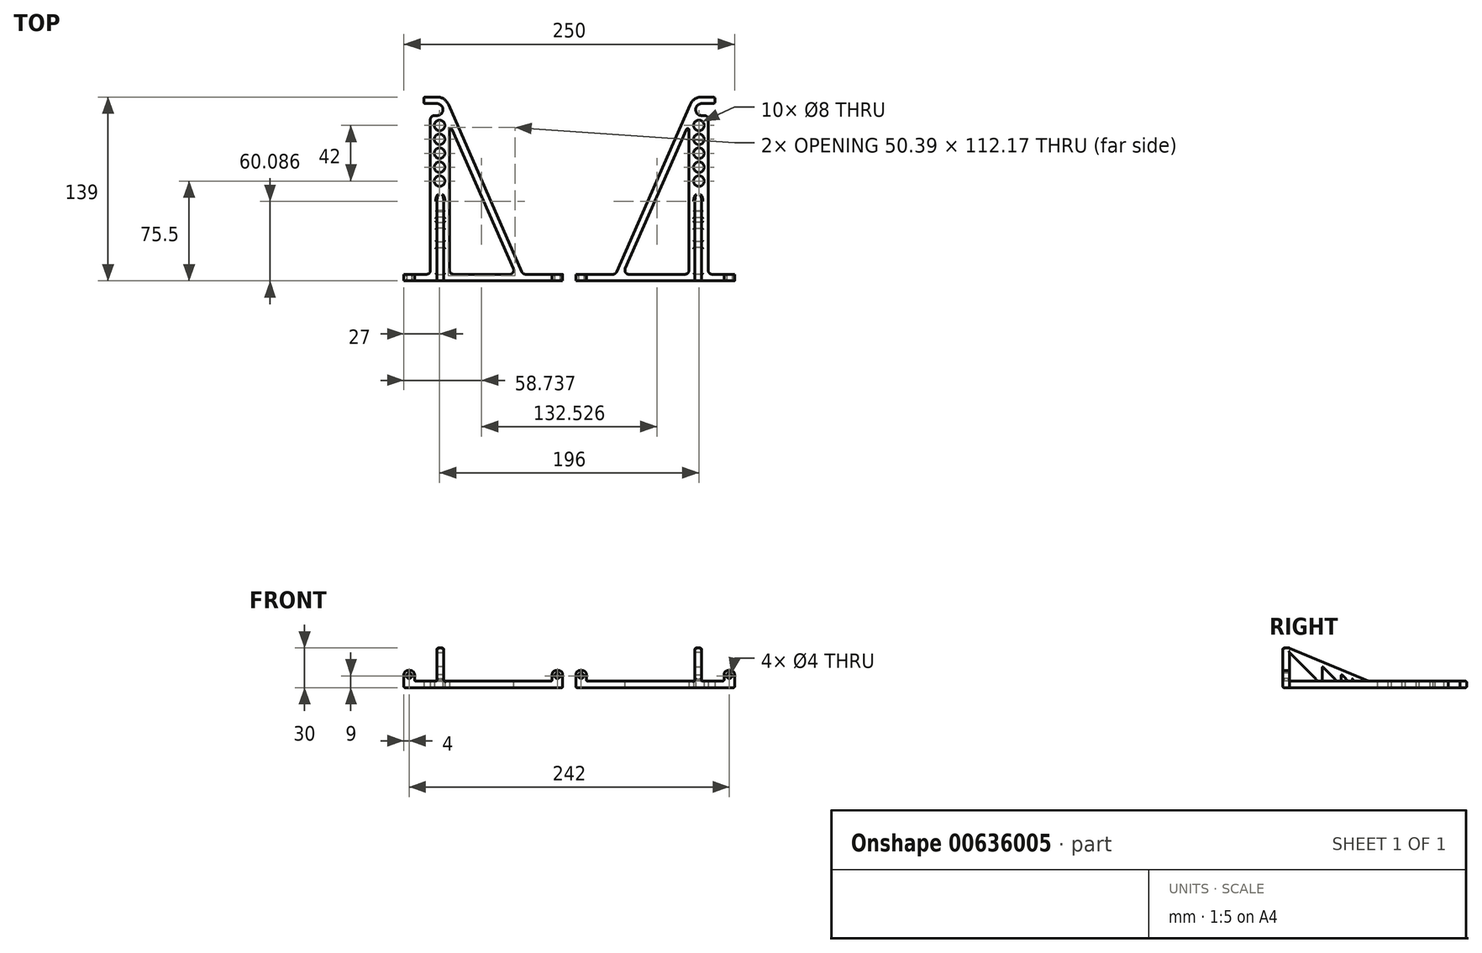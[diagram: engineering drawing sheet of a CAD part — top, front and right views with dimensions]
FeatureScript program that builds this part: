
annotation { "Feature Type Name" : "Feature", "Feature Type Description" : "" }
export const myFeature = defineFeature(function(context is Context, id is Id, definition is map)
    precondition{}
    {
        {
            var Q0;
            Q0=qCreatedBy(makeId("Top.planeOp"),FACE);
            var sketch = newSketch(context, id + "F0", { "sketchPlane" : qUnion([Q0])});
            skLineSegment(sketch, "E0", {"start": v(5, 0) * mm, "end": v(125, 0) * mm});
            skLineSegment(sketch, "E1", {"start": v(5, 0) * mm, "end": v(5, 5) * mm});
            skLineSegment(sketch, "E2", {"start": v(5, 5) * mm, "end": v(35, 5) * mm});
            skLineSegment(sketch, "E3", {"start": v(125, 5) * mm, "end": v(125, 0) * mm});
            skPoint(sketch, "E4", {"position": v(35, 5) * mm});
            skPoint(sketch, "E5", {"position": v(105, 5) * mm});
            skLineSegment(sketch, "E6", {"start": v(105, 5) * mm, "end": v(105, 125) * mm});
            skLineSegment(sketch, "E7", {"start": v(105, 125) * mm, "end": v(100, 125) * mm});
            skPoint(sketch, "E8", {"position": v(100, 134) * mm});
            skArc(sketch, "E9", {"start": v(100, 134) * mm, "mid": v(95.5, 129.5) * mm, "end": v(100, 125) * mm});
            skLineSegment(sketch, "E10", {"start": v(100, 134) * mm, "end": v(110, 134) * mm});
            skLineSegment(sketch, "E11", {"start": v(110, 134) * mm, "end": v(110, 139) * mm});
            skLineSegment(sketch, "E12", {"start": v(110, 139) * mm, "end": v(100, 139) * mm});
            skLineSegment(sketch, "E13", {"start": v(35, 5) * mm, "end": v(91.3, 133.32) * mm});
            skLineSegment(sketch, "E14.trimOffspring", {"start": v(105, 5) * mm, "end": v(125, 5) * mm});
            skArc(sketch, "E15", {"start": v(100, 139) * mm, "mid": v(94.8, 137.45) * mm, "end": v(91.3, 133.32) * mm});
            skLineSegment(sketch, "E16", {"start": v(40.46, 5) * mm, "end": v(90.46, 5) * mm});
            skLineSegment(sketch, "E17", {"start": v(90.46, 5) * mm, "end": v(90.46, 118.96) * mm});
            skLineSegment(sketch, "E18", {"start": v(90.46, 118.96) * mm, "end": v(40.46, 5) * mm});
            skPoint(sketch, "E19", {"position": v(98, 75.5) * mm});
            skCircle(sketch, "E20", {"center": v(98, 75.5) * mm, "radius": 4 * mm});
            skPoint(sketch, "E21", {"position": v(98, 86) * mm});
            skCircle(sketch, "E22", {"center": v(98, 86) * mm, "radius": 4 * mm});
            skPoint(sketch, "E23", {"position": v(98, 96.5) * mm});
            skPoint(sketch, "E24", {"position": v(98, 107) * mm});
            skCircle(sketch, "E25", {"center": v(98, 96.5) * mm, "radius": 4 * mm});
            skCircle(sketch, "E26", {"center": v(98, 107) * mm, "radius": 4 * mm});
            skPoint(sketch, "E27", {"position": v(98, 117.5) * mm});
            skCircle(sketch, "E28", {"center": v(98, 117.5) * mm, "radius": 4 * mm});
            skSolve(sketch);
        }
        {
            var Q0;
            Q0=makeQuery(id+"F0.imprint","IMPRINT",FACE,{"disambiguationData":[TD([[makeQuery(id+"F0.imprint","IMPRINT",EDGE,{"derivedFrom":sQuery(id+"F0.wireOp",EDGE,"E0")}),1.0]])]});
            extrude(context, id + "F1", {"entities" : qUnion([Q0]), "depth" : 5 * mm, "offsetDistance" : 25 * mm});
        }
        {
            var Q0;
            Q0=qCreatedBy(makeId("Front.planeOp"),FACE);
            var sketch = newSketch(context, id + "F2", { "sketchPlane" : qUnion([Q0])});
            skPoint(sketch, "E29", {"position": v(5, 5) * mm});
            skLineSegment(sketch, "E30.bottom", {"start": v(5, 5) * mm, "end": v(13, 5) * mm});
            skLineSegment(sketch, "E30.top", {"start": v(5, 13) * mm, "end": v(13, 13) * mm});
            skLineSegment(sketch, "E30.left", {"start": v(5, 5) * mm, "end": v(5, 13) * mm});
            skLineSegment(sketch, "E30.right", {"start": v(13, 5) * mm, "end": v(13, 13) * mm});
            skPoint(sketch, "E31", {"position": v(125, 5) * mm});
            skPoint(sketch, "E31.positionSnap0", {"position": v(9, 5) * mm});
            skLineSegment(sketch, "E32.bottom", {"start": v(125, 5) * mm, "end": v(117, 5) * mm});
            skLineSegment(sketch, "E32.top", {"start": v(125, 13) * mm, "end": v(117, 13) * mm});
            skLineSegment(sketch, "E32.left", {"start": v(125, 5) * mm, "end": v(125, 13) * mm});
            skLineSegment(sketch, "E32.right", {"start": v(117, 5) * mm, "end": v(117, 13) * mm});
            skPoint(sketch, "E33", {"position": v(9, 9) * mm});
            skPoint(sketch, "E33.positionSnap0", {"position": v(13, 9) * mm});
            skPoint(sketch, "E34", {"position": v(121, 9) * mm});
            skPoint(sketch, "E34.positionSnap0", {"position": v(121, 5) * mm});
            skCircle(sketch, "E35", {"center": v(121, 9) * mm, "radius": 2 * mm});
            skCircle(sketch, "E36", {"center": v(9, 9) * mm, "radius": 2 * mm});
            skPoint(sketch, "E37", {"position": v(100, 5) * mm});
            skLineSegment(sketch, "E38.bottom", {"start": v(100, 5) * mm, "end": v(95, 5) * mm});
            skLineSegment(sketch, "E38.top", {"start": v(100, 30) * mm, "end": v(95, 30) * mm});
            skLineSegment(sketch, "E38.left", {"start": v(100, 5) * mm, "end": v(100, 30) * mm});
            skLineSegment(sketch, "E38.right", {"start": v(95, 5) * mm, "end": v(95, 30) * mm});
            skSolve(sketch);
        }
        {
            var Q0;
            Q0=makeQuery(id+"F2.imprint","IMPRINT",FACE,{"disambiguationData":[TD([[makeQuery(id+"F2.imprint","IMPRINT",EDGE,{"derivedFrom":sQuery(id+"F2.wireOp",EDGE,"E32.bottom")}),-1.0]])]});
            var Q1;
            Q1=makeQuery(id+"F2.imprint","IMPRINT",FACE,{"disambiguationData":[TD([[makeQuery(id+"F2.imprint","IMPRINT",EDGE,{"derivedFrom":sQuery(id+"F2.wireOp",EDGE,"E38.bottom")}),-1.0]])]});
            var Q2;
            Q2=makeQuery(id+"F2.imprint","IMPRINT",FACE,{"disambiguationData":[TD([[makeQuery(id+"F2.imprint","IMPRINT",EDGE,{"derivedFrom":sQuery(id+"F2.wireOp",EDGE,"E30.bottom")}),1.0]])]});
            extrude(context, id + "F3", {"entities" : qUnion([Q0, Q1, Q2]), "operationType" : NewBodyOperationType.ADD, "depth" : -5 * mm, "offsetDistance" : 25 * mm});
        }
        {
            var Q0;
            Q0=qCreatedBy(makeId("Right.planeOp"),FACE);
            var sketch = newSketch(context, id + "F4", { "sketchPlane" : qUnion([Q0])});
            skPoint(sketch, "E39", {"position": v(5, 5) * mm});
            skLineSegment(sketch, "E40", {"start": v(5, 5) * mm, "end": v(65, 5) * mm});
            skLineSegment(sketch, "E41", {"start": v(65, 5) * mm, "end": v(5, 30) * mm});
            skLineSegment(sketch, "E42", {"start": v(5, 30) * mm, "end": v(5, 5) * mm});
            skLineSegment(sketch, "E43", {"start": v(5, 5) * mm, "end": v(5, 26.75) * mm});
            skLineSegment(sketch, "E44", {"start": v(5, 26.75) * mm, "end": v(26.75, 5) * mm});
            skLineSegment(sketch, "E45", {"start": v(26.75, 5) * mm, "end": v(5, 5) * mm});
            skLineSegment(sketch, "E46", {"start": v(29.75, 5) * mm, "end": v(41.19, 5) * mm});
            skLineSegment(sketch, "E47", {"start": v(41.19, 5) * mm, "end": v(29.75, 16.44) * mm});
            skLineSegment(sketch, "E48", {"start": v(29.75, 16.44) * mm, "end": v(29.75, 5) * mm});
            skLineSegment(sketch, "E49", {"start": v(44.19, 5) * mm, "end": v(49.6, 5) * mm});
            skLineSegment(sketch, "E50", {"start": v(49.6, 5) * mm, "end": v(44.19, 10.42) * mm});
            skLineSegment(sketch, "E51", {"start": v(44.19, 10.42) * mm, "end": v(44.19, 5) * mm});
            skLineSegment(sketch, "E52", {"start": v(52.6, 5) * mm, "end": v(54.52, 5) * mm});
            skLineSegment(sketch, "E53", {"start": v(54.52, 5) * mm, "end": v(52.6, 6.91) * mm});
            skLineSegment(sketch, "E54", {"start": v(52.6, 6.91) * mm, "end": v(52.6, 5) * mm});
            skSolve(sketch);
        }
        {
            var Q0;
            Q0=makeQuery(id+"F4.imprint","IMPRINT",FACE,{"disambiguationData":[TD([[makeQuery(id+"F4.imprint","IMPRINT",EDGE,{"derivedFrom":sQuery(id+"F4.wireOp",EDGE,"E40")}),1.0]])]});
            extrude(context, id + "F5", {"entities" : qUnion([Q0]), "operationType" : NewBodyOperationType.ADD, "depth" : 100 * mm, "offsetDistance" : 25 * mm, "hasSecondDirection" : true, "secondDirectionOppositeDirection" : true, "secondDirectionDepth" : -95 * mm});
        }
        {
            var Q0;
            Q0=makeQuery(id+"F3.opExtrude","SWEPT_EDGE",EDGE,{"disambiguationData":[OSD([sQuery(id+"F2.wireOp",EDGE,"E30.top"),sQuery(id+"F2.wireOp",EDGE,"E30.left")])]});
            var Q1;
            Q1=makeQuery(id+"F3.opExtrude","SWEPT_EDGE",EDGE,{"disambiguationData":[OSD([sQuery(id+"F2.wireOp",EDGE,"E30.top"),sQuery(id+"F2.wireOp",EDGE,"E30.right")])]});
            var Q2;
            Q2=makeQuery(id+"F3.opExtrude","SWEPT_EDGE",EDGE,{"disambiguationData":[OSD([sQuery(id+"F2.wireOp",EDGE,"E30.bottom"),sQuery(id+"F2.wireOp",EDGE,"E30.right")])]});
            var Q3;
            Q3=makeQuery(id+"F3.opExtrude","SWEPT_EDGE",EDGE,{"disambiguationData":[OSD([sQuery(id+"F2.wireOp",EDGE,"E32.top"),sQuery(id+"F2.wireOp",EDGE,"E32.right")])]});
            var Q4;
            Q4=makeQuery(id+"F3.opExtrude","SWEPT_EDGE",EDGE,{"disambiguationData":[OSD([sQuery(id+"F2.wireOp",EDGE,"E32.top"),sQuery(id+"F2.wireOp",EDGE,"E32.left")])]});
            var Q5;
            Q5=makeQuery(id+"F3.opExtrude","SWEPT_EDGE",EDGE,{"disambiguationData":[OSD([sQuery(id+"F2.wireOp",EDGE,"E32.bottom"),sQuery(id+"F2.wireOp",EDGE,"E32.right")])]});
            var Q6;
            Q6=makeQuery(id+"F3.opExtrude","SWEPT_EDGE",EDGE,{"disambiguationData":[OSD([sQuery(id+"F2.wireOp",EDGE,"E38.bottom"),sQuery(id+"F2.wireOp",EDGE,"E38.right")])]});
            var Q7;
            Q7=makeQuery(id+"F3.opExtrude","SWEPT_EDGE",EDGE,{"disambiguationData":[OSD([sQuery(id+"F2.wireOp",EDGE,"E38.bottom"),sQuery(id+"F2.wireOp",EDGE,"E38.left")])]});
            var Q8;
            {var subQ0=sQuery(id+"F4.wireOp",EDGE,"E40");Q8=makeQuery(id+"F5.opExtrude","CAP_EDGE",EDGE,{"disambiguationData":[OSD([subQ0]),TDD([makeQuery(id+"F4.imprint","IMPRINT",EDGE,{"disambiguationData":[TD([[makeQuery(id+"F4.imprint","INTERSECT",VERTEX,{"derivedFrom":[subQ0,sQuery(id+"F4.wireOp",EDGE,"E44"),sQuery(id+"F4.wireOp",EDGE,"E45")]}),-1.0]])],"derivedFrom":subQ0})])],"isStart":false});}
            var Q9;
            {var subQ0=sQuery(id+"F4.wireOp",EDGE,"E40");Q9=makeQuery(id+"F5.opExtrude","CAP_EDGE",EDGE,{"disambiguationData":[OSD([subQ0]),TDD([makeQuery(id+"F4.imprint","IMPRINT",EDGE,{"disambiguationData":[TD([[makeQuery(id+"F4.imprint","INTERSECT",VERTEX,{"derivedFrom":[subQ0,sQuery(id+"F4.wireOp",EDGE,"E46"),sQuery(id+"F4.wireOp",EDGE,"E47")]}),-1.0]])],"derivedFrom":subQ0})])],"isStart":false});}
            var Q10;
            {var subQ0=sQuery(id+"F4.wireOp",EDGE,"E40");Q10=makeQuery(id+"F5.opExtrude","CAP_EDGE",EDGE,{"disambiguationData":[OSD([subQ0]),TDD([makeQuery(id+"F4.imprint","IMPRINT",EDGE,{"disambiguationData":[TD([[makeQuery(id+"F4.imprint","INTERSECT",VERTEX,{"derivedFrom":[subQ0,sQuery(id+"F4.wireOp",EDGE,"E49"),sQuery(id+"F4.wireOp",EDGE,"E50")]}),-1.0]])],"derivedFrom":subQ0})])],"isStart":false});}
            var Q11;
            {var subQ0=sQuery(id+"F4.wireOp",EDGE,"E40");Q11=makeQuery(id+"F5.opExtrude","CAP_EDGE",EDGE,{"disambiguationData":[OSD([subQ0]),TDD([makeQuery(id+"F4.imprint","IMPRINT",EDGE,{"disambiguationData":[TD([[makeQuery(id+"F4.imprint","INTERSECT",VERTEX,{"derivedFrom":[subQ0,sQuery(id+"F4.wireOp",EDGE,"E49"),sQuery(id+"F4.wireOp",EDGE,"E50")]}),-1.0]])],"derivedFrom":subQ0})])],"isStart":true});}
            var Q12;
            {var subQ0=sQuery(id+"F4.wireOp",EDGE,"E40");Q12=makeQuery(id+"F5.opExtrude","CAP_EDGE",EDGE,{"disambiguationData":[OSD([subQ0]),TDD([makeQuery(id+"F4.imprint","IMPRINT",EDGE,{"disambiguationData":[TD([[makeQuery(id+"F4.imprint","INTERSECT",VERTEX,{"derivedFrom":[subQ0,sQuery(id+"F4.wireOp",EDGE,"E46"),sQuery(id+"F4.wireOp",EDGE,"E47")]}),-1.0]])],"derivedFrom":subQ0})])],"isStart":true});}
            var Q13;
            {var subQ0=sQuery(id+"F4.wireOp",EDGE,"E40");Q13=makeQuery(id+"F5.opExtrude","CAP_EDGE",EDGE,{"disambiguationData":[OSD([subQ0]),TDD([makeQuery(id+"F4.imprint","IMPRINT",EDGE,{"disambiguationData":[TD([[makeQuery(id+"F4.imprint","INTERSECT",VERTEX,{"derivedFrom":[subQ0,sQuery(id+"F4.wireOp",EDGE,"E44"),sQuery(id+"F4.wireOp",EDGE,"E45")]}),-1.0]])],"derivedFrom":subQ0})])],"isStart":true});}
            var Q14;
            Q14=makeQuery(id+"F1.opExtrude","SWEPT_EDGE",EDGE,{"disambiguationData":[OSD([sQuery(id+"F0.wireOp",EDGE,"E16"),sQuery(id+"F0.wireOp",EDGE,"E17")])]});
            var Q15;
            Q15=makeQuery(id+"F1.opExtrude","SWEPT_EDGE",EDGE,{"disambiguationData":[OSD([sQuery(id+"F0.wireOp",EDGE,"E6"),sQuery(id+"F0.wireOp",EDGE,"E14.trimOffspring")])]});
            var Q16;
            Q16=makeQuery(id+"F1.opExtrude","SWEPT_EDGE",EDGE,{"disambiguationData":[OSD([sQuery(id+"F0.wireOp",EDGE,"E2"),sQuery(id+"F0.wireOp",EDGE,"E13")])]});
            var Q17;
            Q17=makeQuery(id+"F1.opExtrude","SWEPT_EDGE",EDGE,{"disambiguationData":[OSD([sQuery(id+"F0.wireOp",EDGE,"E16"),sQuery(id+"F0.wireOp",EDGE,"E18")])]});
            var Q18;
            Q18=makeQuery(id+"F1.opExtrude","SWEPT_EDGE",EDGE,{"disambiguationData":[OSD([sQuery(id+"F0.wireOp",EDGE,"E6"),sQuery(id+"F0.wireOp",EDGE,"E7")])]});
            fillet(context, id + "F6", {"entities" : qUnion([Q0, Q1, Q2, Q3, Q4, Q5, Q6, Q7, Q8, Q9, Q10, Q11, Q12, Q13, Q14, Q15, Q16, Q17, Q18]), "radius" : 3 * mm, "tangentPropagation" : true, "allowEdgeOverflow" : false});
        }
        {
            var Q0;
            Q0=makeQuery(id+"F5.opExtrude","SWEPT_EDGE",EDGE,{"disambiguationData":[OSD([sQuery(id+"F4.wireOp",EDGE,"E40"),sQuery(id+"F4.wireOp",EDGE,"E52"),sQuery(id+"F4.wireOp",EDGE,"E53")])]});
            var Q1;
            Q1=makeQuery(id+"F5.opExtrude","SWEPT_EDGE",EDGE,{"disambiguationData":[OSD([sQuery(id+"F4.wireOp",EDGE,"E40"),sQuery(id+"F4.wireOp",EDGE,"E52"),sQuery(id+"F4.wireOp",EDGE,"E54")])]});
            var Q2;
            Q2=makeQuery(id+"F5.opExtrude","SWEPT_EDGE",EDGE,{"disambiguationData":[OSD([sQuery(id+"F4.wireOp",EDGE,"E53"),sQuery(id+"F4.wireOp",EDGE,"E54")])]});
            fillet(context, id + "F7", {"entities" : qUnion([Q0, Q1, Q2]), "radius" : 0.1 * mm, "tangentPropagation" : true, "allowEdgeOverflow" : false});
        }
        {
            var Q0;
            Q0=makeQuery(id+"F1.opExtrude","CAP_FACE",FACE,{"disambiguationData":[OSD([sQuery(id+"F0.wireOp",EDGE,"E0"),sQuery(id+"F0.wireOp",EDGE,"E1"),sQuery(id+"F0.wireOp",EDGE,"E2"),sQuery(id+"F0.wireOp",EDGE,"E3"),sQuery(id+"F0.wireOp",EDGE,"E6"),sQuery(id+"F0.wireOp",EDGE,"E7"),sQuery(id+"F0.wireOp",EDGE,"E9"),sQuery(id+"F0.wireOp",EDGE,"E10"),sQuery(id+"F0.wireOp",EDGE,"E11"),sQuery(id+"F0.wireOp",EDGE,"E12"),sQuery(id+"F0.wireOp",EDGE,"E13"),sQuery(id+"F0.wireOp",EDGE,"E14.trimOffspring"),sQuery(id+"F0.wireOp",EDGE,"E15"),sQuery(id+"F0.wireOp",EDGE,"E16"),sQuery(id+"F0.wireOp",EDGE,"E17"),sQuery(id+"F0.wireOp",EDGE,"E18"),sQuery(id+"F0.wireOp",EDGE,"E20"),sQuery(id+"F0.wireOp",EDGE,"E22"),sQuery(id+"F0.wireOp",EDGE,"E25"),sQuery(id+"F0.wireOp",EDGE,"E26"),sQuery(id+"F0.wireOp",EDGE,"E28")])],"isStart":false});
            var Q1;
            Q1=makeQuery(id+"F1.opExtrude","CAP_FACE",FACE,{"disambiguationData":[OSD([sQuery(id+"F0.wireOp",EDGE,"E0"),sQuery(id+"F0.wireOp",EDGE,"E1"),sQuery(id+"F0.wireOp",EDGE,"E2"),sQuery(id+"F0.wireOp",EDGE,"E3"),sQuery(id+"F0.wireOp",EDGE,"E6"),sQuery(id+"F0.wireOp",EDGE,"E7"),sQuery(id+"F0.wireOp",EDGE,"E9"),sQuery(id+"F0.wireOp",EDGE,"E10"),sQuery(id+"F0.wireOp",EDGE,"E11"),sQuery(id+"F0.wireOp",EDGE,"E12"),sQuery(id+"F0.wireOp",EDGE,"E13"),sQuery(id+"F0.wireOp",EDGE,"E14.trimOffspring"),sQuery(id+"F0.wireOp",EDGE,"E15"),sQuery(id+"F0.wireOp",EDGE,"E16"),sQuery(id+"F0.wireOp",EDGE,"E17"),sQuery(id+"F0.wireOp",EDGE,"E18"),sQuery(id+"F0.wireOp",EDGE,"E20"),sQuery(id+"F0.wireOp",EDGE,"E22"),sQuery(id+"F0.wireOp",EDGE,"E25"),sQuery(id+"F0.wireOp",EDGE,"E26"),sQuery(id+"F0.wireOp",EDGE,"E28")])],"isStart":true});
            var Q2;
            Q2=makeQuery(id+"F1.opExtrude","SWEPT_FACE",FACE,{"disambiguationData":[OSD([sQuery(id+"F0.wireOp",EDGE,"E11")])]});
            var Q3;
            Q3=makeQuery(id+"F5.opExtrude","SWEPT_FACE",FACE,{"disambiguationData":[OSD([sQuery(id+"F4.wireOp",EDGE,"E41")])]});
            var Q4;
            Q4=makeQuery(id+"F3.opExtrude","SWEPT_FACE",FACE,{"disambiguationData":[OSD([sQuery(id+"F2.wireOp",EDGE,"E38.top")])]});
            var Q5;
            Q5=makeQuery(id+"F3.opExtrude","SWEPT_FACE",FACE,{"disambiguationData":[OSD([sQuery(id+"F2.wireOp",EDGE,"E35")])]});
            var Q6;
            Q6=makeQuery(id+"F3.opExtrude","SWEPT_FACE",FACE,{"disambiguationData":[OSD([sQuery(id+"F2.wireOp",EDGE,"E36")])]});
            var Q7;
            Q7=makeQuery(id+"F1.opExtrude","SWEPT_EDGE",EDGE,{"disambiguationData":[OSD([sQuery(id+"F0.wireOp",EDGE,"E17"),sQuery(id+"F0.wireOp",EDGE,"E18")])]});
            fillet(context, id + "F8", {"entities" : qUnion([Q0, Q1, Q2, Q3, Q4, Q5, Q6, Q7]), "radius" : 1 * mm, "tangentPropagation" : true, "allowEdgeOverflow" : false});
        }
        {
            var Q0;
            Q0=makeQuery(id+"F5.opExtrude","SWEPT_EDGE",EDGE,{"disambiguationData":[OSD([sQuery(id+"F4.wireOp",EDGE,"E42"),sQuery(id+"F4.wireOp",EDGE,"E43"),sQuery(id+"F4.wireOp",EDGE,"E44")])]});
            var Q1;
            Q1=makeQuery(id+"F5.opExtrude","SWEPT_EDGE",EDGE,{"disambiguationData":[OSD([sQuery(id+"F4.wireOp",EDGE,"E47"),sQuery(id+"F4.wireOp",EDGE,"E48")])]});
            var Q2;
            Q2=makeQuery(id+"F5.opExtrude","SWEPT_EDGE",EDGE,{"disambiguationData":[OSD([sQuery(id+"F4.wireOp",EDGE,"E50"),sQuery(id+"F4.wireOp",EDGE,"E51")])]});
            var Q3;
            Q3=makeQuery(id+"F5.boolean.opBoolean","MERGE",FACE,{"derivedFrom":[makeQuery(id+"F3.opExtrude","SWEPT_FACE",FACE,{"disambiguationData":[OSD([sQuery(id+"F2.wireOp",EDGE,"E38.left")])]}),makeQuery(id+"F5.opExtrude","CAP_FACE",FACE,{"disambiguationData":[OSD([sQuery(id+"F4.wireOp",EDGE,"E40"),sQuery(id+"F4.wireOp",EDGE,"E41"),sQuery(id+"F4.wireOp",EDGE,"E42"),sQuery(id+"F4.wireOp",EDGE,"E44"),sQuery(id+"F4.wireOp",EDGE,"E47"),sQuery(id+"F4.wireOp",EDGE,"E48"),sQuery(id+"F4.wireOp",EDGE,"E50"),sQuery(id+"F4.wireOp",EDGE,"E51"),sQuery(id+"F4.wireOp",EDGE,"E53"),sQuery(id+"F4.wireOp",EDGE,"E54")])],"isStart":false})]});
            var Q4;
            Q4=makeQuery(id+"F5.boolean.opBoolean","MERGE",FACE,{"derivedFrom":[makeQuery(id+"F3.opExtrude","SWEPT_FACE",FACE,{"disambiguationData":[OSD([sQuery(id+"F2.wireOp",EDGE,"E38.right")])]}),makeQuery(id+"F5.opExtrude","CAP_FACE",FACE,{"disambiguationData":[OSD([sQuery(id+"F4.wireOp",EDGE,"E40"),sQuery(id+"F4.wireOp",EDGE,"E41"),sQuery(id+"F4.wireOp",EDGE,"E42"),sQuery(id+"F4.wireOp",EDGE,"E44"),sQuery(id+"F4.wireOp",EDGE,"E47"),sQuery(id+"F4.wireOp",EDGE,"E48"),sQuery(id+"F4.wireOp",EDGE,"E50"),sQuery(id+"F4.wireOp",EDGE,"E51"),sQuery(id+"F4.wireOp",EDGE,"E53"),sQuery(id+"F4.wireOp",EDGE,"E54")])],"isStart":true})]});
            fillet(context, id + "F9", {"entities" : qUnion([Q0, Q1, Q2, Q3, Q4]), "radius" : 0.5 * mm, "tangentPropagation" : true, "allowEdgeOverflow" : false});
        }
        {
            var Q0;
            Q0=makeQuery(id+"F1.opExtrude","SWEPT_BODY",BODY,{"disambiguationData":[OSD([sQuery(id+"F0.wireOp",EDGE,"E0"),sQuery(id+"F0.wireOp",EDGE,"E1"),sQuery(id+"F0.wireOp",EDGE,"E2"),sQuery(id+"F0.wireOp",EDGE,"E3"),sQuery(id+"F0.wireOp",EDGE,"E6"),sQuery(id+"F0.wireOp",EDGE,"E7"),sQuery(id+"F0.wireOp",EDGE,"E9"),sQuery(id+"F0.wireOp",EDGE,"E10"),sQuery(id+"F0.wireOp",EDGE,"E11"),sQuery(id+"F0.wireOp",EDGE,"E12"),sQuery(id+"F0.wireOp",EDGE,"E13"),sQuery(id+"F0.wireOp",EDGE,"E14.trimOffspring"),sQuery(id+"F0.wireOp",EDGE,"E15"),sQuery(id+"F0.wireOp",EDGE,"E16"),sQuery(id+"F0.wireOp",EDGE,"E17"),sQuery(id+"F0.wireOp",EDGE,"E18"),sQuery(id+"F0.wireOp",EDGE,"E20"),sQuery(id+"F0.wireOp",EDGE,"E22"),sQuery(id+"F0.wireOp",EDGE,"E25"),sQuery(id+"F0.wireOp",EDGE,"E26"),sQuery(id+"F0.wireOp",EDGE,"E28")])]});
            var Q1;
            Q1=qCreatedBy(makeId("Right.planeOp"),FACE);
            mirror(context, id + "F10", {"entities" : qUnion([Q0]), "mirrorPlane" : qUnion([Q1])});
        }
    });
